# Revit family: Grab_Bar-Gamco-150C.MBLK_Series
name_source: partatom
category: Specialty Equipment
units: mm (PartAtom-declared; Revit-internal decimal feet)

## family parameters
Cut with Voids When Loaded = No
Host = Face
OmniClass Number = 23.40.20.21.47
OmniClass Title = Bath Grab Bars
Part Type = Normal
Room Calculation Point = No
Round Connector Dimension = Use Diameter
Shared = Yes

## types (5) — shared parameters
-C for concealed flange = Yes
ADA Compliant = Yes
Assembly Code = C1030200
Concealed Flange Material = Metal-Bobrick-Stainless Steel
Default Elevation = 0"
Description = Straight Grab Bar with Concealed Flange, Matte Black
Flange Diameter = 3"
Flange Thickness = 1/2"
Installation Type = Wall Mounted
L1 = 1/8"
Manufacturer = Bobrick
Material = Stainless Steel-Bobrick-Matte Black
Mounting Height = 33"
Mounting Height Constraint = 33"
Mounting Plate Material = Metal-Bobrick-Stainless Steel
Product Documentation Link = https://www.bobrick.com
Product Page URL = https://www.bobrick.com
R1 = 3/4"
R2 = 2 1/4"
Tube Diameter = 1 1/2"
Tubing Material = Stainless Steel-Bobrick-Matte Black
URL = https://www.bobrick.com
Wall Clearance = 1 1/2"
Wall to Grab Bar Gap = 1 1/2"
Warranty Documentation Link = https://www.bobrick.com

## per-type parameters (varying)
| type | Length |
| 150Cx24.MBLK | 24" |
| 150Cx36.MBLK | 36" |
| 150Cx42.MBLK | 42" |
| 150Cx48.MBLK | 48" |
| 150Cx18.MBLK | 18" |

note: column(s) folded — value = type name in every type: Model

## geometry (parser evidence)
native form markers: Sweep x3
no freeform markers — native parametric forms only
